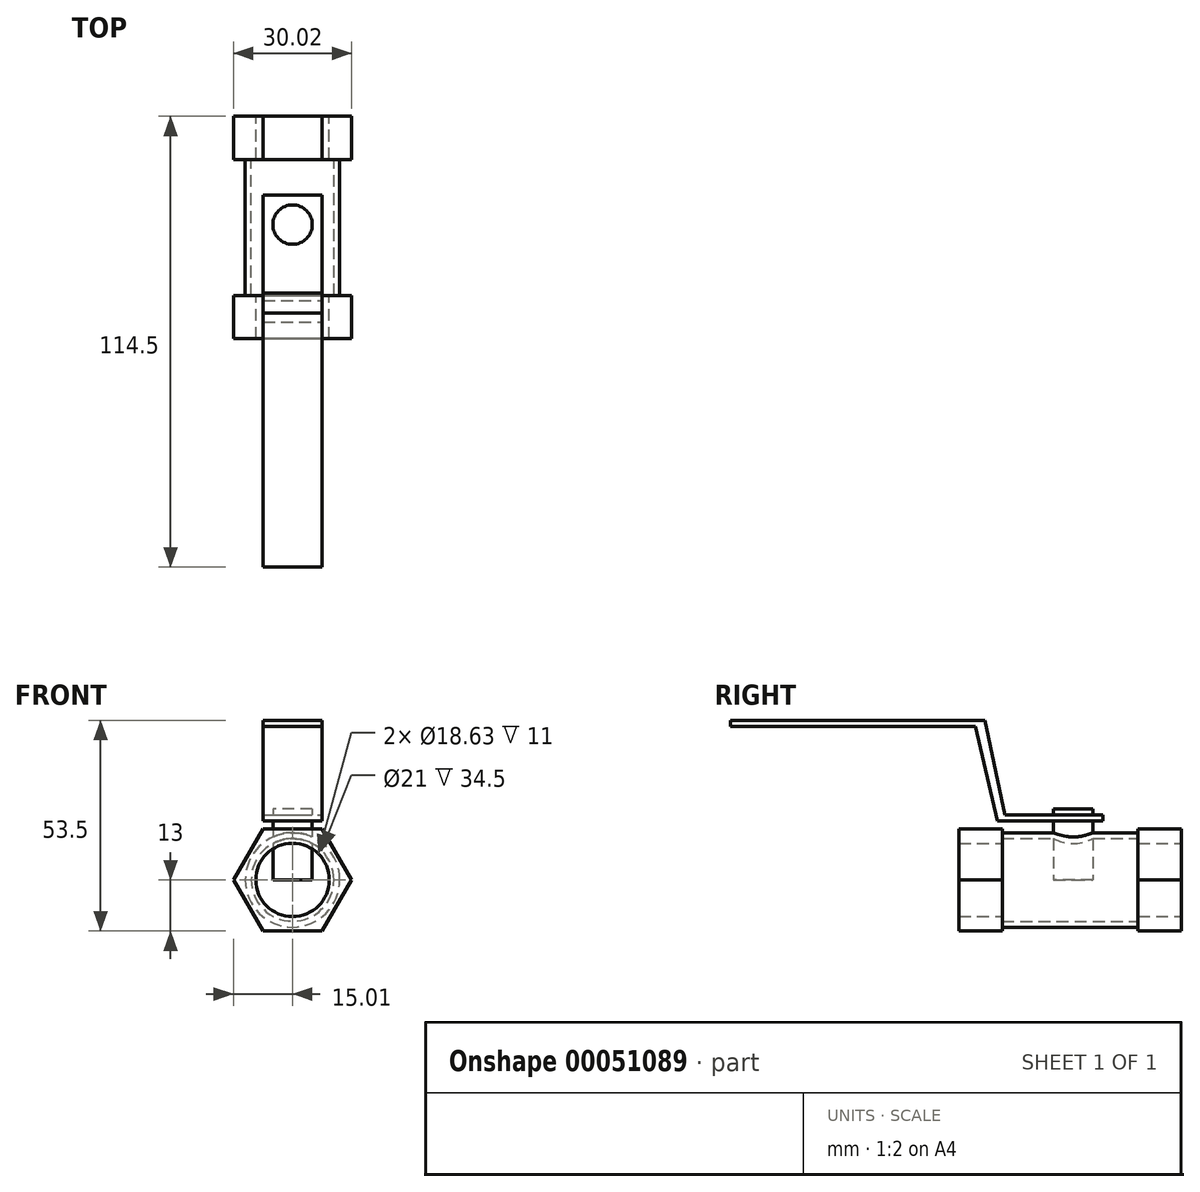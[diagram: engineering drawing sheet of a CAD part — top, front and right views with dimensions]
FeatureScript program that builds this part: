
annotation { "Feature Type Name" : "Feature", "Feature Type Description" : "" }
export const myFeature = defineFeature(function(context is Context, id is Id, definition is map)
    precondition{}
    {
        {
            var Q0;
            Q0=qCreatedBy(makeId("Front.planeOp"),FACE);
            var sketch = newSketch(context, id + "F0", { "sketchPlane" : qUnion([Q0])});
            skCircle(sketch, "E0", {"center": v(0, 0) * mm, "radius": 9.32 * mm});
            skCircle(sketch, "E1.cCircle", {"center": v(0, 0) * mm, "radius": 13 * mm, "construction": true});
            skLineSegment(sketch, "E1.0", {"start": v(-15.01, 0) * mm, "end": v(-7.5, 13) * mm});
            skLineSegment(sketch, "E1.1", {"start": v(-7.5, 13) * mm, "end": v(7.5, 13) * mm});
            skLineSegment(sketch, "E1.2", {"start": v(7.5, 13) * mm, "end": v(15.01, 0) * mm});
            skLineSegment(sketch, "E1.3", {"start": v(15.01, 0) * mm, "end": v(7.5, -13) * mm});
            skLineSegment(sketch, "E1.4", {"start": v(7.5, -13) * mm, "end": v(-7.5, -13) * mm});
            skLineSegment(sketch, "E1.5", {"start": v(-7.5, -13) * mm, "end": v(-15.01, 0) * mm});
            skPoint(sketch, "E1.0.midPoint", {"position": v(-11.26, 6.5) * mm});
            skSolve(sketch);
        }
        {
            var Q0;
            Q0=qSketchRegion(id+"F0",true);
            extrude(context, id + "F1", {"entities" : qUnion([Q0]), "depth" : 11 * mm});
        }
        {
            var Q0;
            Q0=makeQuery(id+"F1.opExtrude","CAP_FACE",FACE,{"disambiguationData":[OSD([sQuery(id+"F0.wireOp",EDGE,"E0"),sQuery(id+"F0.wireOp",EDGE,"E1.0"),sQuery(id+"F0.wireOp",EDGE,"E1.1"),sQuery(id+"F0.wireOp",EDGE,"E1.2"),sQuery(id+"F0.wireOp",EDGE,"E1.3"),sQuery(id+"F0.wireOp",EDGE,"E1.4"),sQuery(id+"F0.wireOp",EDGE,"E1.5")])],"isStart":false});
            var sketch = newSketch(context, id + "F2", { "sketchPlane" : qUnion([Q0])});
            skCircle(sketch, "E2", {"center": v(0, 0) * mm, "radius": 10.5 * mm});
            skCircle(sketch, "E3", {"center": v(0, 0) * mm, "radius": 12 * mm});
            skSolve(sketch);
        }
        {
            var Q0;
            Q0=qSketchRegion(id+"F2",true);
            extrude(context, id + "F3", {"entities" : qUnion([Q0]), "operationType" : NewBodyOperationType.ADD, "depth" : (56.5 - 22) * mm});
        }
        {
            var Q0;
            Q0=makeQuery(id+"F3.opExtrude","CAP_FACE",FACE,{"disambiguationData":[OSD([sQuery(id+"F2.wireOp",EDGE,"E2"),sQuery(id+"F2.wireOp",EDGE,"E3")])],"isStart":false});
            var sketch = newSketch(context, id + "F4", { "sketchPlane" : qUnion([Q0])});
            skCircle(sketch, "E4", {"center": v(0, 0) * mm, "radius": 9.32 * mm});
            skCircle(sketch, "E5.cCircle", {"center": v(0, 0) * mm, "radius": 13 * mm, "construction": true});
            skLineSegment(sketch, "E5.0", {"start": v(-15.01, 0) * mm, "end": v(-7.5, 13) * mm});
            skLineSegment(sketch, "E5.1", {"start": v(-7.5, 13) * mm, "end": v(7.5, 13) * mm});
            skLineSegment(sketch, "E5.2", {"start": v(7.5, 13) * mm, "end": v(15.01, 0) * mm});
            skLineSegment(sketch, "E5.3", {"start": v(15.01, 0) * mm, "end": v(7.5, -13) * mm});
            skLineSegment(sketch, "E5.4", {"start": v(7.5, -13) * mm, "end": v(-7.5, -13) * mm});
            skLineSegment(sketch, "E5.5", {"start": v(-7.5, -13) * mm, "end": v(-15.01, 0) * mm});
            skPoint(sketch, "E5.0.midPoint", {"position": v(-11.26, 6.5) * mm});
            skSolve(sketch);
        }
        {
            var Q0;
            Q0=qSketchRegion(id+"F4",true);
            extrude(context, id + "F5", {"entities" : qUnion([Q0]), "operationType" : NewBodyOperationType.ADD, "depth" : 11 * mm});
        }
        {
            var Q0;
            Q0=qCreatedBy(makeId("Top.planeOp"),FACE);
            var sketch = newSketch(context, id + "F6", { "sketchPlane" : qUnion([Q0])});
            skCircle(sketch, "E6", {"center": v(0, -27.5) * mm, "radius": 5 * mm});
            skSolve(sketch);
        }
        {
            var Q0;
            Q0=qSketchRegion(id+"F6",true);
            extrude(context, id + "F7", {"entities" : qUnion([Q0]), "operationType" : NewBodyOperationType.ADD, "depth" : 18 * mm});
        }
        {
            var Q0;
            Q0=qCreatedBy(makeId("Right.planeOp"),FACE);
            var sketch = newSketch(context, id + "F8", { "sketchPlane" : qUnion([Q0])});
            skLineSegment(sketch, "E7", {"start": v(-20, 16.5) * mm, "end": v(-20, 15) * mm});
            skLineSegment(sketch, "E8", {"start": v(-20, 15) * mm, "end": v(-46.76, 15) * mm});
            skLineSegment(sketch, "E9", {"start": v(-46.76, 15) * mm, "end": v(-52.3, 39) * mm});
            skLineSegment(sketch, "E10", {"start": v(-52.3, 39) * mm, "end": v(-114.5, 39) * mm});
            skLineSegment(sketch, "E11", {"start": v(-114.5, 39) * mm, "end": v(-114.5, 40.5) * mm});
            skLineSegment(sketch, "E12", {"start": v(-114.5, 40.5) * mm, "end": v(-49.95, 40.5) * mm});
            skLineSegment(sketch, "E13", {"start": v(-49.95, 40.5) * mm, "end": v(-44.84, 16.5) * mm});
            skLineSegment(sketch, "E14", {"start": v(-44.84, 16.5) * mm, "end": v(-20, 16.5) * mm});
            skSolve(sketch);
        }
        {
            var Q0;
            Q0=qSketchRegion(id+"F8",true);
            extrude(context, id + "F9", {"entities" : qUnion([Q0]), "operationType" : NewBodyOperationType.ADD, "endBound" : BoundingType.SYMMETRIC, "oppositeDirection" : true, "depth" : 15 * mm});
        }
    });
